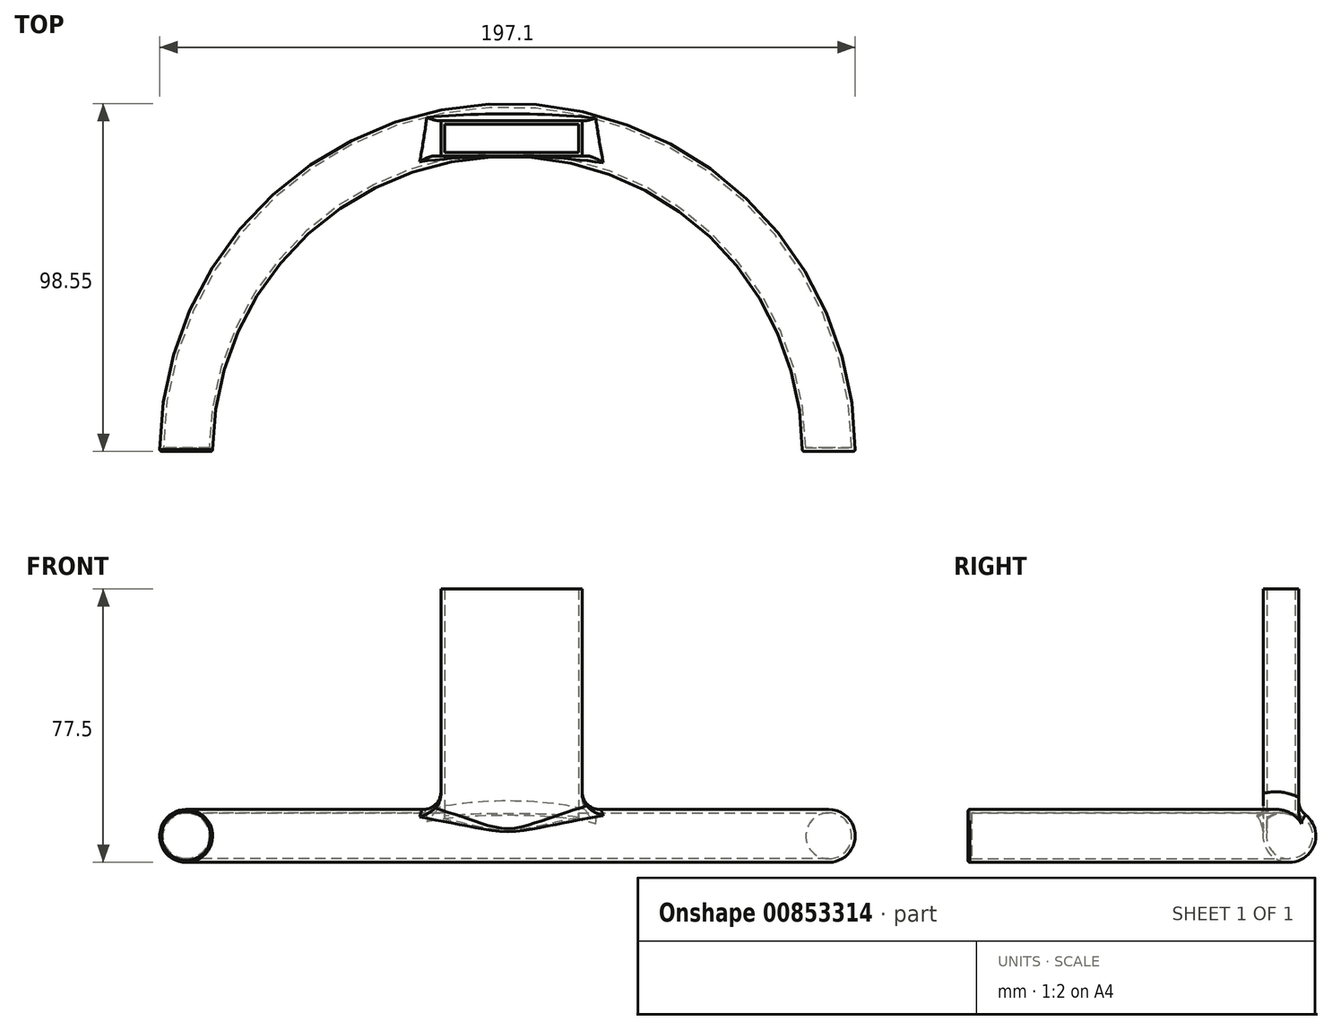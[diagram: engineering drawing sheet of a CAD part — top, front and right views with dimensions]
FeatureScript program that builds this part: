
annotation { "Feature Type Name" : "Feature", "Feature Type Description" : "" }
export const myFeature = defineFeature(function(context is Context, id is Id, definition is map)
    precondition{}
    {
        {
            var Q0;
            Q0=qCreatedBy(makeId("Top.planeOp"),FACE);
            var sketch = newSketch(context, id + "F0", { "sketchPlane" : qUnion([Q0])});
            skArc(sketch, "E0", {"start": v(225, 0) * mm, "mid": v(0, 225) * mm, "end": v(-225, 0) * mm});
            skPoint(sketch, "E1.orphan", {"position": v(-282.37, 0) * mm});
            skSolve(sketch);
        }
        {
            var Q0;
            Q0=qCreatedBy(makeId("Front.planeOp"),FACE);
            var sketch = newSketch(context, id + "F1", { "sketchPlane" : qUnion([Q0])});
            skCircle(sketch, "E2", {"center": v(-91.05, 0) * mm, "radius": 7.5 * mm});
            skSolve(sketch);
        }
        {
            var Q0;
            Q0=makeQuery(id+"F1.imprint","IMPRINT",FACE,{"disambiguationData":[TD([[makeQuery(id+"F1.imprint","IMPRINT",EDGE,{"derivedFrom":sQuery(id+"F1.wireOp",EDGE,"E2")}),1.0]])]});
            var Q1;
            Q1=sQuery(id+"F0.wireOp",EDGE,"E0");
            sweep(context, id + "F2", {"profiles" : qUnion([Q0]), "path" : qUnion([Q1])});
        }
        {
            var Q0;
            Q0=qCreatedBy(makeId("Top.planeOp"),FACE);
            var sketch = newSketch(context, id + "F3", { "sketchPlane" : qUnion([Q0])});
            skLineSegment(sketch, "E3.bottom", {"start": v(-18.86, 93.72) * mm, "end": v(21.14, 93.72) * mm});
            skLineSegment(sketch, "E3.top", {"start": v(-18.86, 83.72) * mm, "end": v(21.14, 83.72) * mm});
            skLineSegment(sketch, "E3.left", {"start": v(-18.86, 93.72) * mm, "end": v(-18.86, 83.72) * mm});
            skLineSegment(sketch, "E3.right", {"start": v(21.14, 93.72) * mm, "end": v(21.14, 83.72) * mm});
            skSolve(sketch);
        }
        {
            var Q0;
            Q0 = qSketchRegion(id + "F3", true);
            extrude(context, id + "F4", {"entities" : qUnion([Q0]), "operationType" : NewBodyOperationType.ADD, "depth" : 70 * mm, "offsetDistance" : 25 * mm});
        }
        {
            var Q0;
            Q0=makeQuery(id+"F4.opExtrude","CAP_FACE",FACE,{"disambiguationData":[OSD([sQuery(id+"F3.wireOp",EDGE,"E3.bottom"),sQuery(id+"F3.wireOp",EDGE,"E3.top"),sQuery(id+"F3.wireOp",EDGE,"E3.left"),sQuery(id+"F3.wireOp",EDGE,"E3.right")])],"isStart":false});
            shell(context, id + "F5", {"entities" : qUnion([Q0]), "thickness" : 1 * mm});
        }
        {
            var Q0;
            Q0=makeQuery(id+"F4.boolean.opBoolean","INTERSECT",EDGE,{"derivedFrom":[makeQuery(id+"F2.opSweep","SWEPT_FACE",FACE,{"disambiguationData":[OSD([sQuery(id+"F0.wireOp",EDGE,"E0"),sQuery(id+"F1.wireOp",EDGE,"E2")])]}),makeQuery(id+"F4.opExtrude","SWEPT_FACE",FACE,{"disambiguationData":[OSD([sQuery(id+"F3.wireOp",EDGE,"E3.bottom")])]})]});
            var Q1;
            Q1=makeQuery(id+"F4.boolean.opBoolean","INTERSECT",EDGE,{"derivedFrom":[makeQuery(id+"F2.opSweep","SWEPT_FACE",FACE,{"disambiguationData":[OSD([sQuery(id+"F0.wireOp",EDGE,"E0"),sQuery(id+"F1.wireOp",EDGE,"E2")])]}),makeQuery(id+"F4.opExtrude","SWEPT_FACE",FACE,{"disambiguationData":[OSD([sQuery(id+"F3.wireOp",EDGE,"E3.left")])]})]});
            var Q2;
            Q2=makeQuery(id+"F4.boolean.opBoolean","INTERSECT",EDGE,{"derivedFrom":[makeQuery(id+"F2.opSweep","SWEPT_FACE",FACE,{"disambiguationData":[OSD([sQuery(id+"F0.wireOp",EDGE,"E0"),sQuery(id+"F1.wireOp",EDGE,"E2")])]}),makeQuery(id+"F4.opExtrude","SWEPT_FACE",FACE,{"disambiguationData":[OSD([sQuery(id+"F3.wireOp",EDGE,"E3.right")])]})]});
            var Q3;
            Q3=makeQuery(id+"F4.boolean.opBoolean","INTERSECT",EDGE,{"derivedFrom":[makeQuery(id+"F2.opSweep","SWEPT_FACE",FACE,{"disambiguationData":[OSD([sQuery(id+"F0.wireOp",EDGE,"E0"),sQuery(id+"F1.wireOp",EDGE,"E2")])]}),makeQuery(id+"F4.opExtrude","SWEPT_FACE",FACE,{"disambiguationData":[OSD([sQuery(id+"F3.wireOp",EDGE,"E3.top")])]})]});
            fillet(context, id + "F6", {"entities" : qUnion([Q0, Q1, Q2, Q3]), "radius" : 5 * mm, "tangentPropagation" : true, "allowEdgeOverflow" : false});
        }
        {
            var Q0;
            Q0=makeQuery(id+"F2.opSweep","CAP_EDGE",EDGE,{"disambiguationData":[OSD([sQuery(id+"F0.wireOp",VERTEX,"E0.start"),sQuery(id+"F1.wireOp",EDGE,"E2")])],"isStart":false});
            fillet(context, id + "F7", {"entities" : qUnion([Q0]), "radius" : 0.5 * mm, "tangentPropagation" : true, "allowEdgeOverflow" : false});
        }
        {
            var Q0;
            Q0=makeQuery(id+"F2.opSweep","CAP_FACE",FACE,{"disambiguationData":[OSD([sQuery(id+"F0.wireOp",VERTEX,"E0.end"),sQuery(id+"F1.wireOp",EDGE,"E2")])],"isStart":true});
            fillet(context, id + "F8", {"entities" : qUnion([Q0]), "radius" : 0.5 * mm, "tangentPropagation" : true, "allowEdgeOverflow" : false});
        }
    });
